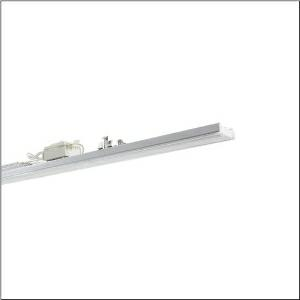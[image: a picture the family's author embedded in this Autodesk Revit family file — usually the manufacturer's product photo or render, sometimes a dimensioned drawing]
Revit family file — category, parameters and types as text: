
# Revit family: licross_11_recessed_mo_51te19cn485g
name_source: partatom
category: Lighting Fixtures
units: mm (PartAtom-declared; Revit-internal decimal feet)

## family parameters
Cut with Voids When Loaded = No
Host = Face
Light Source = No
Part Type = Normal
Room Calculation Point = No
Round Connector Dimension = Use Diameter
Shared = No

## types (1)
- --- (1 x LED, 8920 lm, 49.3 W, 4000K)
    Apparent Load = 49 VA
    CIE Flux Codes = 55 90 98 100 100
    Color Rendering = 80
    Color Temperature = 4000K
    Default Elevation = 1800 mm
    Description = Licross 11 Recessed MO, luminaire insert, of sheet steel, galvanised, coil coated, white, length: 1.500mm, width: 66mm, height: 67mm, LED rated luminous flux: 8.920lm, light colour: 840, SDCM (Standard Deviation of Colour Matching)MacAdam ≤ 2 SDCM (initial), control gear: ON/OFF Multilumen, CLOi, with plug, 3-pole, with phase selection, mains connection: 220..240V, AC, 50/60Hz, start of lifetime: 49W, end of service life: 55W, internal wiring halogen-free, primary light control with lens, of plastic, primary optical cover: cover, of PMMA, light emission: direct distribution, primary light characteristic: double asymmetric, protection rating (complete): IP54, insulation class (complete): insulation class I (protective earthing), certification: CE, ENEC, VDE, UKCA, protection symbol: D if used in an environment with non-conductive dust loads with corresponding accessories, impact resistance: IK06, permissible ambient temperature for indoor applications: -35..+40°C, corresponds to IFS (International Featured Standards) requirements for safety and quality in the food industry, reducing of maximum allowable ambient temperature of 5°C with ceiling mounting, LABS conformity tested according to VDMA 24364:2018-05, The light source and the operating device comply with the requirements of the Ecodesign Regulation (EU) 2019/2020 and are replaceable in accordance with this regulation, packaging unit: 1 piece
    Height = 58 mm
    Lamp = 1 x LED
    Lamp Light Flux = 8920 lm
    Lamp Power = 49.3 W
    Lamp count = 1
    Length = 1500 mm
    Luminous efficacy = 181 lm/W
    Manufacturer = Siteco
    ModVariant = No
    Model = 51TE19CN485G
    Mounting Place = Ceiling
    Mounting Type = Pendant
    Number of Poles = 1
    OnlyDefault = Yes
    Power Factor = 1
    Product Name = Licross 11 Recessed MO
    Product group = luminaire insert | ceiling pendant
    ProductGroupID = 901
    Protection Class = Protection class I
    Protection Degree = IP 54
    RLX_Detail_Level = 1
    RLX_Emergency_Light_Flux = 0 lm
    RLX_Emergency_Type = 0
    RLX_Emergency_Type_DB = No
    RlxData = <blob elided: 22637 chars, md5=7eee30ef>
    Socket = socket
    Standby Power = 0 W
    System Light Flux = 8920 lm
    System Power = 49 W
    Type Comments = factory setting: luminous flux: 100 % | (A | C | E) | 113 mA
    Type Image = l_1296930.jpg
    URL = http://relux.com
    VarID = @adj_090953
    Voltage = 0 V
    Weight = 0.00 kg
    Width = 66 mm

## geometry (parser evidence)
native form markers: Blend x4, Sweep x11
no freeform markers — native parametric forms only
